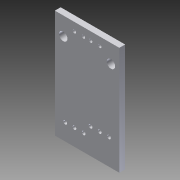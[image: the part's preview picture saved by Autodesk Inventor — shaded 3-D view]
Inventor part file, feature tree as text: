
AUTODESK INVENTOR PART (.ipt)
format: ipt  version: 2014 SP1 (Build 180222100, 222)  size: 87,552 bytes
history: native  units: in
note: dims shown in document units (in); Inventor stores cm internally (conversion verified against a paired STEP export)
features: extrude x1, imported_body x1
ambient origin geometry x8: Origin, YZ Plane, XZ Plane, XY Plane, X Axis, Y Axis, Z Axis, Center Point
bodies: Body1 (feature_tree)
feature tree (2):
  extrude  "Extrude3"  [1 undecoded]
  imported_body  "Base1"
note: 1 required parameter value undecoded (feature->parameter linkage not recoverable at this tier; creation-order binding heuristic only, values carry confidence <= 0.55)
